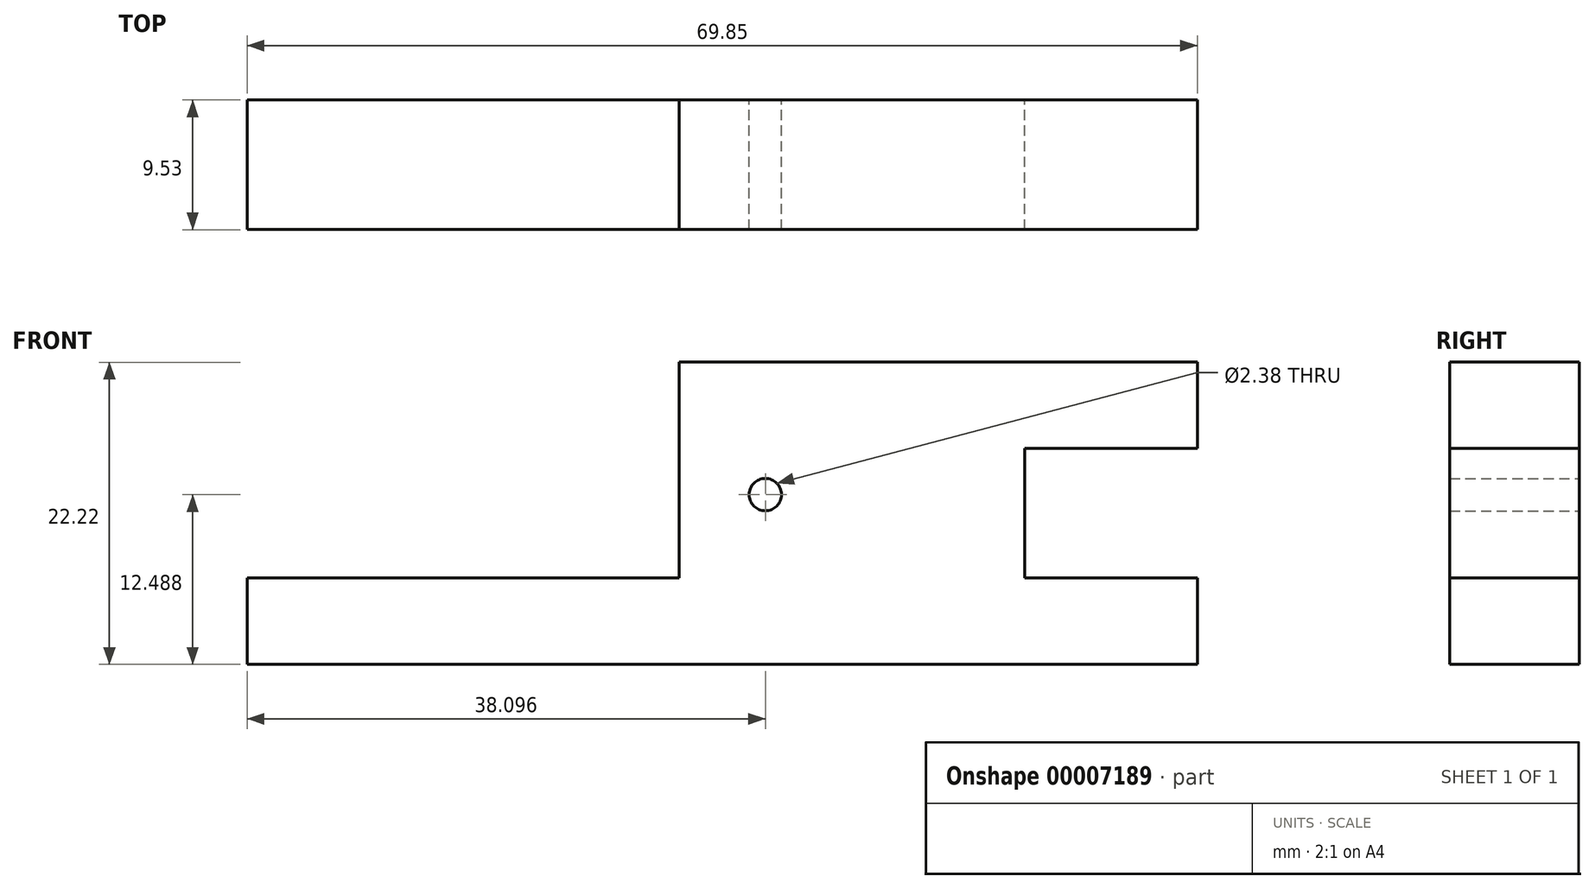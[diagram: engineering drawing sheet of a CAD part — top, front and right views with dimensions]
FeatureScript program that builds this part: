
annotation { "Feature Type Name" : "Feature", "Feature Type Description" : "" }
export const myFeature = defineFeature(function(context is Context, id is Id, definition is map)
    precondition{}
    {
        {
            var Q0;
            Q0=qCreatedBy(makeId("Front.planeOp"),FACE);
            var sketch = newSketch(context, id + "F0", { "sketchPlane" : qUnion([Q0])});
            skLineSegment(sketch, "E0", {"start": v(-52.71, 4.36) * mm, "end": v(-52.71, -2) * mm});
            skLineSegment(sketch, "E1", {"start": v(-52.71, -2) * mm, "end": v(17.14, -2) * mm});
            skLineSegment(sketch, "E2", {"start": v(17.14, -2) * mm, "end": v(17.14, 4.36) * mm});
            skLineSegment(sketch, "E3", {"start": v(17.14, 4.36) * mm, "end": v(4.44, 4.36) * mm});
            skLineSegment(sketch, "E4", {"start": v(4.44, 4.36) * mm, "end": v(4.44, 13.88) * mm});
            skLineSegment(sketch, "E5", {"start": v(4.44, 13.88) * mm, "end": v(17.14, 13.88) * mm});
            skLineSegment(sketch, "E6", {"start": v(17.14, 13.88) * mm, "end": v(17.14, 20.23) * mm});
            skLineSegment(sketch, "E7", {"start": v(17.14, 20.23) * mm, "end": v(-20.96, 20.23) * mm});
            skLineSegment(sketch, "E8", {"start": v(-20.96, 20.23) * mm, "end": v(-20.96, 4.36) * mm});
            skLineSegment(sketch, "E9", {"start": v(-20.96, 4.36) * mm, "end": v(-52.71, 4.36) * mm});
            skCircle(sketch, "E10", {"center": v(-14.61, 10.5) * mm, "radius": 1.2 * mm});
            skSolve(sketch);
        }
        {
            var Q0;
            Q0=makeQuery(id+"F0.imprint","IMPRINT",FACE,{"disambiguationData":[TD([[makeQuery(id+"F0.imprint","IMPRINT",EDGE,{"derivedFrom":sQuery(id+"F0.wireOp",EDGE,"E0")}),1.0]])]});
            extrude(context, id + "F1", {"entities" : qUnion([Q0]), "depth" : 9.52 * mm});
        }
    });
